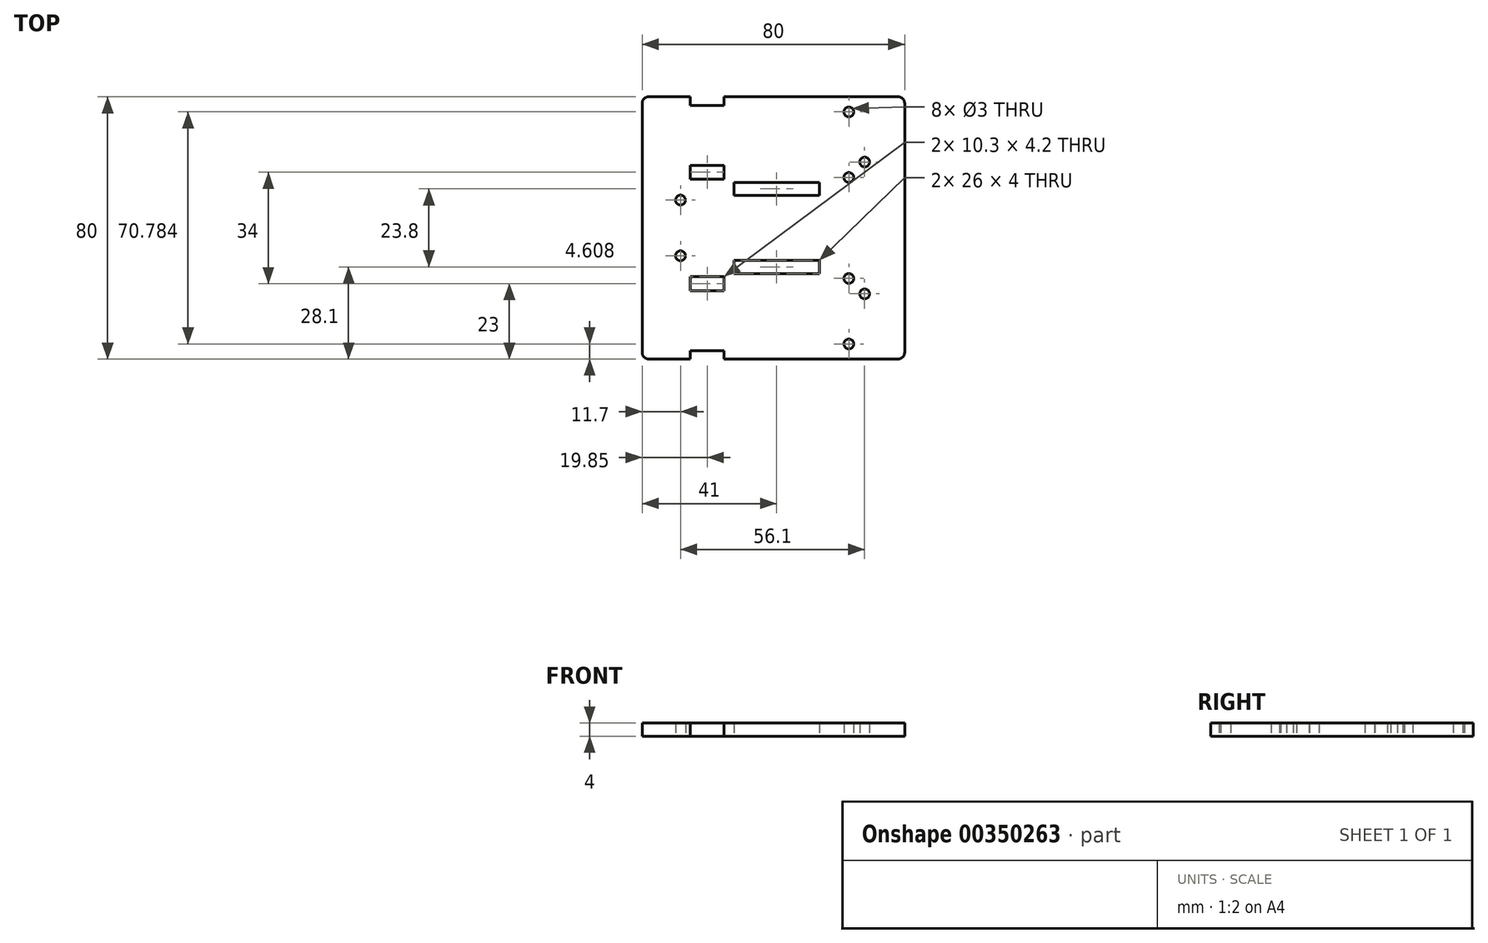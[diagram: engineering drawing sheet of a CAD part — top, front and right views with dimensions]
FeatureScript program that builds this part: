
annotation { "Feature Type Name" : "Feature", "Feature Type Description" : "" }
export const myFeature = defineFeature(function(context is Context, id is Id, definition is map)
    precondition{}
    {
        {
            var Q0;
            Q0=qCreatedBy(makeId("Top.planeOp"),FACE);
            var sketch = newSketch(context, id + "F0", { "sketchPlane" : qUnion([Q0])});
            skLineSegment(sketch, "E0", {"start": v(-50, 0) * mm, "end": v(-50, 38) * mm});
            skLineSegment(sketch, "E1", {"start": v(-48, 40) * mm, "end": v(-35.3, 40) * mm});
            skLineSegment(sketch, "E2", {"start": v(-35.3, 40) * mm, "end": v(-35.3, 37.4) * mm});
            skLineSegment(sketch, "E3", {"start": v(-35.3, 37.4) * mm, "end": v(-25, 37.4) * mm});
            skLineSegment(sketch, "E4", {"start": v(-25, 37.4) * mm, "end": v(-25, 40) * mm});
            skLineSegment(sketch, "E5", {"start": v(-25, 40) * mm, "end": v(28, 40) * mm});
            skLineSegment(sketch, "E6", {"start": v(30, 38) * mm, "end": v(30, 0) * mm});
            skLineSegment(sketch, "E7", {"start": v(-35.3, 40) * mm, "end": v(-35.3, 0) * mm, "construction": true});
            skLineSegment(sketch, "E8", {"start": v(-25, 37.4) * mm, "end": v(-25, 0) * mm, "construction": true});
            skLineSegment(sketch, "E9.bottom", {"start": v(-35.3, 19.1) * mm, "end": v(-25, 19.1) * mm});
            skLineSegment(sketch, "E9.top", {"start": v(-35.3, 14.9) * mm, "end": v(-25, 14.9) * mm});
            skLineSegment(sketch, "E9.left", {"start": v(-35.3, 19.1) * mm, "end": v(-35.3, 14.9) * mm});
            skLineSegment(sketch, "E9.right", {"start": v(-25, 19.1) * mm, "end": v(-25, 14.9) * mm});
            skCircle(sketch, "E10", {"center": v(-38.3, 8.5) * mm, "radius": 1.5 * mm});
            skCircle(sketch, "E11", {"center": v(17.8, 20.1) * mm, "radius": 1.5 * mm});
            skLineSegment(sketch, "E12.MirrorCS", {"start": v(-25, -37.4) * mm, "end": v(-25, -40) * mm});
            skLineSegment(sketch, "E13.MirrorCS", {"start": v(-35.3, -40) * mm, "end": v(-35.3, -37.4) * mm});
            skLineSegment(sketch, "E14.MirrorCS", {"start": v(-25, -19.1) * mm, "end": v(-25, -14.9) * mm});
            skLineSegment(sketch, "E15.MirrorCS", {"start": v(-35.3, -19.1) * mm, "end": v(-35.3, -14.9) * mm});
            skLineSegment(sketch, "E16.MirrorCS", {"start": v(30, -38) * mm, "end": v(30, 0) * mm});
            skCircle(sketch, "E17.MirrorC", {"center": v(-38.3, -8.5) * mm, "radius": 1.5 * mm});
            skLineSegment(sketch, "E18.MirrorCS", {"start": v(-25, -40) * mm, "end": v(28, -40) * mm});
            skLineSegment(sketch, "E19.MirrorCS", {"start": v(-48, -40) * mm, "end": v(-35.3, -40) * mm});
            skLineSegment(sketch, "E20.MirrorCS", {"start": v(-35.3, -14.9) * mm, "end": v(-25, -14.9) * mm});
            skLineSegment(sketch, "E21.MirrorCS", {"start": v(-35.3, -40) * mm, "end": v(-35.3, 0) * mm, "construction": true});
            skLineSegment(sketch, "E22.MirrorCS", {"start": v(-25, -37.4) * mm, "end": v(-25, 0) * mm, "construction": true});
            skLineSegment(sketch, "E23.MirrorCS", {"start": v(-35.3, -19.1) * mm, "end": v(-25, -19.1) * mm});
            skCircle(sketch, "E24.MirrorC", {"center": v(17.8, -20.1) * mm, "radius": 1.5 * mm});
            skLineSegment(sketch, "E25.MirrorCS", {"start": v(-35.3, -37.4) * mm, "end": v(-25, -37.4) * mm});
            skLineSegment(sketch, "E26.MirrorCS", {"start": v(-50, 0) * mm, "end": v(-50, -38) * mm});
            skPoint(sketch, "E27.visualSharp", {"position": v(-50, 40) * mm});
            skArc(sketch, "E27.filletArc", {"start": v(-48, 40) * mm, "mid": v(-49.41, 39.41) * mm, "end": v(-50, 38) * mm});
            skPoint(sketch, "E28.visualSharp", {"position": v(30, 40) * mm});
            skArc(sketch, "E28.filletArc", {"start": v(30, 38) * mm, "mid": v(29.41, 39.41) * mm, "end": v(28, 40) * mm});
            skPoint(sketch, "E29.visualSharp", {"position": v(30, -40) * mm});
            skArc(sketch, "E29.filletArc", {"start": v(28, -40) * mm, "mid": v(29.41, -39.41) * mm, "end": v(30, -38) * mm});
            skPoint(sketch, "E30.visualSharp", {"position": v(-50, -40) * mm});
            skArc(sketch, "E30.filletArc", {"start": v(-50, -38) * mm, "mid": v(-49.41, -39.41) * mm, "end": v(-48, -40) * mm});
            skLineSegment(sketch, "E31.bottom", {"start": v(-22, 13.9) * mm, "end": v(4, 13.9) * mm});
            skLineSegment(sketch, "E31.top", {"start": v(-22, 9.9) * mm, "end": v(4, 9.9) * mm});
            skLineSegment(sketch, "E31.left", {"start": v(-22, 13.9) * mm, "end": v(-22, 9.9) * mm});
            skLineSegment(sketch, "E31.right", {"start": v(4, 13.9) * mm, "end": v(4, 9.9) * mm});
            skLineSegment(sketch, "E32.MirrorCS", {"start": v(-22, -13.9) * mm, "end": v(-22, -9.9) * mm});
            skLineSegment(sketch, "E33.MirrorCS", {"start": v(-22, -13.9) * mm, "end": v(4, -13.9) * mm});
            skLineSegment(sketch, "E34.MirrorCS", {"start": v(4, -13.9) * mm, "end": v(4, -9.9) * mm});
            skLineSegment(sketch, "E35.MirrorCS", {"start": v(-22, -9.9) * mm, "end": v(4, -9.9) * mm});
            skCircle(sketch, "E36", {"center": v(13, 15.4) * mm, "radius": 1.5 * mm});
            skCircle(sketch, "E37.MirrorC", {"center": v(13, -15.4) * mm, "radius": 1.5 * mm});
            skCircle(sketch, "E38", {"center": v(13, 35.4) * mm, "radius": 1.5 * mm});
            skCircle(sketch, "E39.MirrorC", {"center": v(13, -35.4) * mm, "radius": 1.5 * mm});
            skSolve(sketch);
        }
        {
            var Q0;
            Q0 = qSketchRegion(id + "F0", true);
            extrude(context, id + "F1", {"entities" : qUnion([Q0]), "depth" : 4 * mm});
        }
    });
